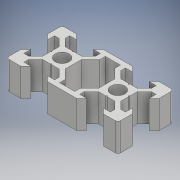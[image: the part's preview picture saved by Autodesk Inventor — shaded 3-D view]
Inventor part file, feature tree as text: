
AUTODESK INVENTOR PART (.ipt)
format: ipt  version: 2018 (Build 220112000, 112)  size: 205,312 bytes
history: native  units: mm
features: other x1, extrude x1, sketch x1
ambient origin geometry x8: Origin, YZ Plane, XZ Plane, XY Plane, X Axis, Y Axis, Z Axis, Center Point
bodies: Body1 (feature_tree)
feature tree (3):
  other  "Sólido1"
  extrude  "Extrusão1"  [1 undecoded]
  sketch  "Esboço1"  dims[d0=10.0mm d1=0.0mm]
note: 1 required parameter value undecoded (feature->parameter linkage not recoverable at this tier; creation-order binding heuristic only, values carry confidence <= 0.55)
